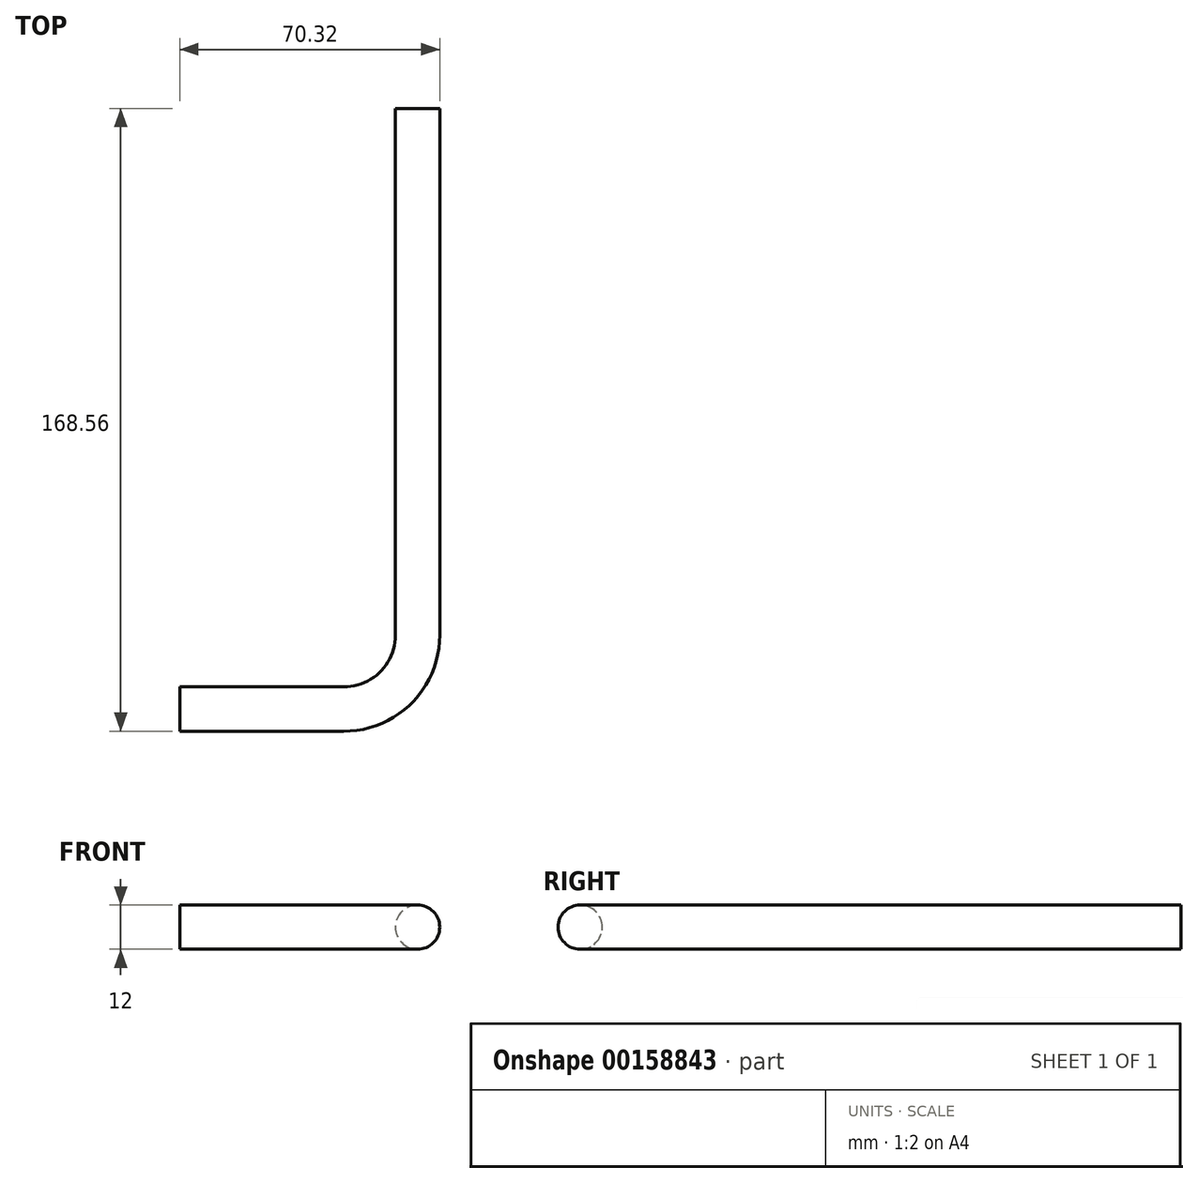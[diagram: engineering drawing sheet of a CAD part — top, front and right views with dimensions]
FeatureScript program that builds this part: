
annotation { "Feature Type Name" : "Feature", "Feature Type Description" : "" }
export const myFeature = defineFeature(function(context is Context, id is Id, definition is map)
    precondition{}
    {
        {
            var Q0;
            Q0=qCreatedBy(makeId("Top.planeOp"),FACE);
            var sketch = newSketch(context, id + "F0", { "sketchPlane" : qUnion([Q0])});
            skLineSegment(sketch, "E0", {"start": v(0, 0) * mm, "end": v(44.32, 0) * mm});
            skLineSegment(sketch, "E1", {"start": v(64.32, 20) * mm, "end": v(64.32, 162.56) * mm});
            skPoint(sketch, "E2.visualSharp", {"position": v(64.32, 0) * mm});
            skArc(sketch, "E2.filletArc", {"start": v(44.32, 0) * mm, "mid": v(58.46, 5.86) * mm, "end": v(64.32, 20) * mm});
            skSolve(sketch);
        }
        {
            var Q0;
            Q0=qCreatedBy(makeId("Right.planeOp"),FACE);
            var sketch = newSketch(context, id + "F1", { "sketchPlane" : qUnion([Q0])});
            skCircle(sketch, "E3", {"center": v(0, 0) * mm, "radius": 6 * mm});
            skSolve(sketch);
        }
        {
            var Q0;
            Q0=makeQuery(id+"F1.imprint","IMPRINT",FACE,{"disambiguationData":[TD([[makeQuery(id+"F1.imprint","IMPRINT",EDGE,{"derivedFrom":sQuery(id+"F1.wireOp",EDGE,"E3")}),1.0]])]});
            var Q1;
            Q1=sQuery(id+"F0.wireOp",EDGE,"E0");
            var Q2;
            Q2=sQuery(id+"F0.wireOp",EDGE,"E2.filletArc");
            var Q3;
            Q3=sQuery(id+"F0.wireOp",EDGE,"E1");
            sweep(context, id + "F2", {"profiles" : qUnion([Q0]), "path" : qUnion([Q1, Q2, Q3])});
        }
    });
